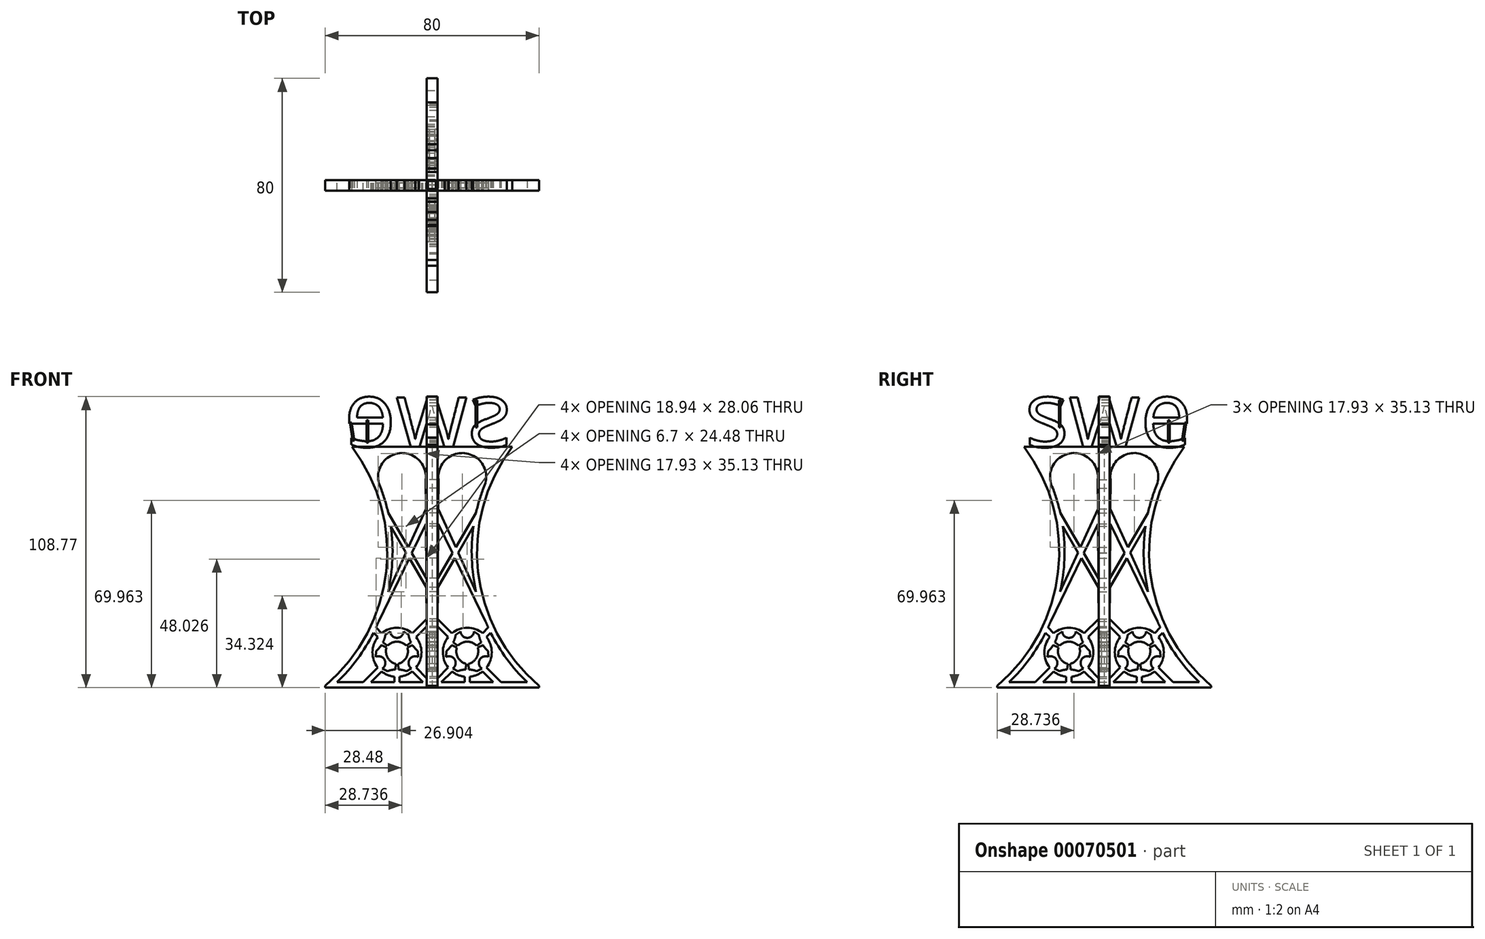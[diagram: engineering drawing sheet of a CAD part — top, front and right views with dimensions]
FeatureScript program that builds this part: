
annotation { "Feature Type Name" : "Feature", "Feature Type Description" : "" }
export const myFeature = defineFeature(function(context is Context, id is Id, definition is map)
    precondition{}
    {
        {
            var Q0;
            Q0=qCreatedBy(makeId("Right.planeOp"),FACE);
            var sketch = newSketch(context, id + "F0", { "sketchPlane" : qUnion([Q0])});
            skLineSegment(sketch, "E0", {"start": v(-30, 90) * mm, "end": v(0, 90) * mm});
            skLineSegment(sketch, "E1", {"start": v(0, 90) * mm, "end": v(0, 0) * mm});
            skLineSegment(sketch, "E2", {"start": v(0, 0) * mm, "end": v(-40, 0) * mm});
            skLineSegment(sketch, "E3", {"start": v(-40, 0) * mm, "end": v(-40, 0.68) * mm});
            skArc(sketch, "E4", {"start": v(-40, 0.68) * mm, "mid": v(-17.2, 43.35) * mm, "end": v(-30, 90) * mm});
            skArc(sketch, "E5", {"start": v(-6.02, 7.42) * mm, "mid": v(-4, 13.15) * mm, "end": v(-6.01, 18.88) * mm});
            skArc(sketch, "E6.0", {"start": v(-35.54, 2) * mm, "mid": v(-27.93, 10.66) * mm, "end": v(-21.9, 20.5) * mm});
            skLineSegment(sketch, "E6.1", {"start": v(-2, 2) * mm, "end": v(-12.16, 2) * mm});
            skLineSegment(sketch, "E7", {"start": v(-25.73, 2) * mm, "end": v(-20.3, 7.43) * mm});
            skLineSegment(sketch, "E8", {"start": v(-22.9, 2) * mm, "end": v(-18.89, 6.02) * mm});
            skLineSegment(sketch, "E9", {"start": v(-2, 3.4) * mm, "end": v(-6.02, 7.42) * mm});
            skLineSegment(sketch, "E10", {"start": v(-3.42, 2) * mm, "end": v(-7.43, 6.01) * mm});
            skLineSegment(sketch, "E11.trimOffspring", {"start": v(-7.42, 20.3) * mm, "end": v(-2.05, 25.66) * mm});
            skLineSegment(sketch, "E12.trimOffspring", {"start": v(-6.01, 18.88) * mm, "end": v(-2, 22.89) * mm});
            skLineSegment(sketch, "E13.trimOffspring", {"start": v(-18.88, 20.3) * mm, "end": v(-20.99, 22.4) * mm});
            skLineSegment(sketch, "E14.trimOffspring", {"start": v(-20.3, 18.89) * mm, "end": v(-21.9, 20.5) * mm});
            skArc(sketch, "E15.trimOffspring", {"start": v(-18.89, 6.02) * mm, "mid": v(-16.66, 4.7) * mm, "end": v(-14.16, 4.05) * mm});
            skArc(sketch, "E16.trimOffspring", {"start": v(-20.3, 18.89) * mm, "mid": v(-22.31, 13.16) * mm, "end": v(-20.3, 7.43) * mm});
            skArc(sketch, "E17.trimOffspring", {"start": v(-7.42, 20.3) * mm, "mid": v(-13.15, 22.31) * mm, "end": v(-18.88, 20.3) * mm});
            skLineSegment(sketch, "E18.trimOffspring", {"start": v(-2, 22.89) * mm, "end": v(-2, 2) * mm});
            skLineSegment(sketch, "E19", {"start": v(-14.16, 4.05) * mm, "end": v(-14.16, 2) * mm});
            skLineSegment(sketch, "E20", {"start": v(-12.16, 4.05) * mm, "end": v(-12.16, 2) * mm});
            skPoint(sketch, "E20.startSnap0", {"position": v(-14.16, 4.05) * mm});
            skArc(sketch, "E21.trimOffspring", {"start": v(-12.16, 4.05) * mm, "mid": v(-9.65, 4.7) * mm, "end": v(-7.43, 6.01) * mm});
            skLineSegment(sketch, "E22.trimOffspring", {"start": v(-14.16, 2) * mm, "end": v(-35.54, 2) * mm});
            skLineSegment(sketch, "E23", {"start": v(-25.35, 13.16) * mm, "end": v(3.04, 13.16) * mm, "construction": true});
            skLineSegment(sketch, "E24", {"start": v(-13.16, 13.16) * mm, "end": v(-0.47, 22.2) * mm, "construction": true});
            skLineSegment(sketch, "E25", {"start": v(-13.16, 13.16) * mm, "end": v(-2.45, 29.33) * mm, "construction": true});
            skLineSegment(sketch, "E26", {"start": v(-13.16, 13.16) * mm, "end": v(-8.24, 28.3) * mm, "construction": true});
            skLineSegment(sketch, "E27", {"start": v(-9.65, 15.66) * mm, "end": v(-7.9, 16.9) * mm});
            skLineSegment(sketch, "E28", {"start": v(-10.64, 20.91) * mm, "end": v(-8.82, 19.7) * mm});
            skArc(sketch, "E29", {"start": v(-8.82, 19.7) * mm, "mid": v(-8.49, 18.27) * mm, "end": v(-7.9, 16.9) * mm});
            skLineSegment(sketch, "E30", {"start": v(-13.16, 13.16) * mm, "end": v(-18.41, 16.9) * mm, "construction": true});
            skLineSegment(sketch, "E31", {"start": v(-13.16, 13.16) * mm, "end": v(-18.55, 21.3) * mm, "construction": true});
            skLineSegment(sketch, "E32", {"start": v(-13.16, 13.16) * mm, "end": v(-16.83, 24.47) * mm, "construction": true});
            skLineSegment(sketch, "E33", {"start": v(-16.66, 15.66) * mm, "end": v(-18.41, 16.9) * mm});
            skLineSegment(sketch, "E34", {"start": v(-15.68, 20.91) * mm, "end": v(-17.5, 19.7) * mm});
            skArc(sketch, "E35", {"start": v(-15.68, 20.91) * mm, "mid": v(-13.16, 18.56) * mm, "end": v(-10.64, 20.91) * mm});
            skArc(sketch, "E36", {"start": v(-18.41, 16.9) * mm, "mid": v(-17.83, 18.27) * mm, "end": v(-17.5, 19.7) * mm});
            skArc(sketch, "E37", {"start": v(-9.65, 15.66) * mm, "mid": v(-13.16, 17.16) * mm, "end": v(-16.66, 15.66) * mm});
            skLineSegment(sketch, "E38", {"start": v(-25.53, 20.8) * mm, "end": v(-2.82, 20.8) * mm, "construction": true});
            skLineSegment(sketch, "E39", {"start": v(-16.66, 15.66) * mm, "end": v(-2.86, 15.66) * mm, "construction": true});
            skArc(sketch, "E40.1.0", {"start": v(-18.61, 7.1) * mm, "mid": v(-17.84, 10.45) * mm, "end": v(-21.13, 11.46) * mm});
            skLineSegment(sketch, "E40.1.1", {"start": v(-18.61, 7.1) * mm, "end": v(-16.66, 6.12) * mm});
            skArc(sketch, "E40.1.2", {"start": v(-13.77, 6.72) * mm, "mid": v(-15.25, 6.56) * mm, "end": v(-16.66, 6.12) * mm});
            skLineSegment(sketch, "E40.1.3", {"start": v(-13.57, 8.86) * mm, "end": v(-13.77, 6.72) * mm});
            skArc(sketch, "E40.1.4", {"start": v(-17.08, 14.94) * mm, "mid": v(-16.62, 11.15) * mm, "end": v(-13.57, 8.86) * mm});
            skLineSegment(sketch, "E40.1.5", {"start": v(-17.08, 14.94) * mm, "end": v(-19.03, 15.83) * mm});
            skArc(sketch, "E40.1.6", {"start": v(-21, 13.64) * mm, "mid": v(-19.92, 14.64) * mm, "end": v(-19.03, 15.83) * mm});
            skLineSegment(sketch, "E40.1.7", {"start": v(-21.13, 11.46) * mm, "end": v(-21, 13.64) * mm});
            skArc(sketch, "E40.2.0", {"start": v(-5.18, 11.46) * mm, "mid": v(-8.47, 10.45) * mm, "end": v(-7.7, 7.1) * mm});
            skLineSegment(sketch, "E40.2.1", {"start": v(-5.18, 11.46) * mm, "end": v(-5.31, 13.64) * mm});
            skArc(sketch, "E40.2.2", {"start": v(-7.28, 15.83) * mm, "mid": v(-6.4, 14.64) * mm, "end": v(-5.31, 13.64) * mm});
            skLineSegment(sketch, "E40.2.3", {"start": v(-9.23, 14.94) * mm, "end": v(-7.28, 15.83) * mm});
            skArc(sketch, "E40.2.4", {"start": v(-12.74, 8.86) * mm, "mid": v(-9.7, 11.15) * mm, "end": v(-9.23, 14.94) * mm});
            skLineSegment(sketch, "E40.2.5", {"start": v(-12.74, 8.86) * mm, "end": v(-12.54, 6.72) * mm});
            skArc(sketch, "E40.2.6", {"start": v(-9.65, 6.12) * mm, "mid": v(-11.06, 6.56) * mm, "end": v(-12.54, 6.72) * mm});
            skLineSegment(sketch, "E40.2.7", {"start": v(-7.7, 7.1) * mm, "end": v(-9.65, 6.12) * mm});
            skLineSegment(sketch, "E41", {"start": v(-2.37, 77.68) * mm, "end": v(-2.14, 40.93) * mm});
            skArc(sketch, "E42.trimOffspring", {"start": v(-35.54, 2) * mm, "mid": v(-26.56, 12.58) * mm, "end": v(-19.95, 24.78) * mm});
            skArc(sketch, "E43", {"start": v(-2.37, 77.68) * mm, "mid": v(-12.93, 87.53) * mm, "end": v(-19.17, 74.5) * mm});
            skLineSegment(sketch, "E44", {"start": v(-16.45, 35.79) * mm, "end": v(-9.74, 50.45) * mm});
            skLineSegment(sketch, "E45", {"start": v(-2.27, 61.23) * mm, "end": v(-7.6, 50.24) * mm});
            skLineSegment(sketch, "E46", {"start": v(-16.42, 65.3) * mm, "end": v(-8.86, 52.4) * mm});
            skLineSegment(sketch, "E47", {"start": v(-2.12, 37.44) * mm, "end": v(-8.51, 48.35) * mm});
            skArc(sketch, "E48.trimOffspring", {"start": v(-16.42, 65.3) * mm, "mid": v(-17.63, 69.95) * mm, "end": v(-19.17, 74.5) * mm});
            skLineSegment(sketch, "E49.trimOffspring", {"start": v(-8.86, 52.4) * mm, "end": v(-2.3, 66.74) * mm});
            skLineSegment(sketch, "E50.trimOffspring", {"start": v(-9.74, 50.45) * mm, "end": v(-15.49, 60.26) * mm});
            skLineSegment(sketch, "E51.trimOffspring", {"start": v(-7.6, 50.24) * mm, "end": v(-2.14, 40.93) * mm});
            skLineSegment(sketch, "E52.trimOffspring", {"start": v(-2.12, 37.44) * mm, "end": v(-2.05, 25.66) * mm});
            skArc(sketch, "E53.trimOffspring", {"start": v(-16.45, 35.79) * mm, "mid": v(-14.85, 47.98) * mm, "end": v(-15.49, 60.26) * mm});
            skLineSegment(sketch, "E54.trimOffspring", {"start": v(-8.51, 48.35) * mm, "end": v(-19.95, 24.78) * mm});
            skSolve(sketch);
        }
        {
            var Q0;
            Q0=qSketchRegion(id+"F0",true);
            extrude(context, id + "F1", {"entities" : qUnion([Q0]), "depth" : 2 * mm, "hasSecondDirection" : true, "secondDirectionOppositeDirection" : true, "secondDirectionDepth" : 2 * mm});
        }
        {
            var Q0;
            Q0=qCreatedBy(makeId("Right.planeOp"),FACE);
            var sketch = newSketch(context, id + "F2", { "sketchPlane" : qUnion([Q0])});
            skLineSegment(sketch, "E55", {"start": v(0, 81) * mm, "end": v(0, -28.5) * mm, "construction": true});
            skSolve(sketch);
        }
        {
            var Q0;
            Q0=makeQuery(id+"F1.opExtrude","SWEPT_BODY",BODY,{"disambiguationData":[OSD([sQuery(id+"F0.wireOp",EDGE,"E0"),sQuery(id+"F0.wireOp",EDGE,"E1"),sQuery(id+"F0.wireOp",EDGE,"N8EfN9Iy-VFxy-i62X-S3Tn-et34u0hB6ofw"),sQuery(id+"F0.wireOp",EDGE,"ofOerVMI-8AtS-AqWo-Xm8z-ZVAlB3EUovam"),sQuery(id+"F0.wireOp",EDGE,"ba3e6201-bb00-4176-be12-0bcf97df4df2"),sQuery(id+"F0.wireOp",EDGE,"k6Ju8hmT-RXya-gFIe-6RDm-fDKX84Fwp2G4"),sQuery(id+"F0.wireOp",EDGE,"dTDJtstR-zKxY-rc8w-sIGn-4ASnDpw26A23"),sQuery(id+"F0.wireOp",EDGE,"Cvr0LfUC-tO0D-IxcI-B5Ti-WW2sAGeSHFF8"),sQuery(id+"F0.wireOp",EDGE,"DwRJblST-1CEV-pcTT-NFQT-YytcCcE5cTGx"),sQuery(id+"F0.wireOp",EDGE,"973229ff-babc-457a-ac66-6eeaf75bea45")])]});
            var Q1;
            Q1=sQuery(id+"F2.wireOp",EDGE,"E55");
            circularPattern(context, id + "F3", {"entities" : qUnion([Q0]), "axis" : qUnion([Q1]), "angle" : 90 * degree, "instanceCount" : round(4)});
        }
        {
            var Q0;
            Q0=qCreatedBy(makeId("Right.planeOp"),FACE);
            var sketch = newSketch(context, id + "F4", { "sketchPlane" : qUnion([Q0])});
            skText(sketch, "E56", { "text": "swe", "fontName": "OpenSans-Regular.ttf"});
            skLineSegment(sketch, "E57", {"start": v(-2.01, 88.78) * mm, "end": v(-2.01, 87.76) * mm, "construction": true});
            skLineSegment(sketch, "E58", {"start": v(2.01, 88.85) * mm, "end": v(2.01, 87.7) * mm, "construction": true});
            skLineSegment(sketch, "E59", {"start": v(-2.01, 88.27) * mm, "end": v(0, 88.27) * mm, "construction": true});
            skPoint(sketch, "E59.endSnap0", {"position": v(-2.01, 88.27) * mm});
            skLineSegment(sketch, "E60", {"start": v(0, 88.27) * mm, "end": v(2.01, 88.27) * mm, "construction": true});
            skLineSegment(sketch, "E61", {"start": v(0, 88.27) * mm, "end": v(0, 111.2) * mm, "construction": true});
            const initialGuessF4  = {"E56": [-0.0297, 0.09, 1, 0, 0.0248]};
            skSetInitialGuess(sketch, initialGuessF4);
            skSolve(sketch);
        }
        {
            var Q0;
            Q0=qSketchRegion(id+"F4",true);
            var Q1;
            Q1=makeQuery(id+"F1.opExtrude","CAP_FACE",FACE,{"disambiguationData":[OSD([sQuery(id+"F0.wireOp",EDGE,"E0"),sQuery(id+"F0.wireOp",EDGE,"E1"),sQuery(id+"F0.wireOp",EDGE,"E2"),sQuery(id+"F0.wireOp",EDGE,"E3"),sQuery(id+"F0.wireOp",EDGE,"E4"),sQuery(id+"F0.wireOp",EDGE,"E5"),sQuery(id+"F0.wireOp",EDGE,"E6.1"),sQuery(id+"F0.wireOp",EDGE,"E7"),sQuery(id+"F0.wireOp",EDGE,"E8"),sQuery(id+"F0.wireOp",EDGE,"E9"),sQuery(id+"F0.wireOp",EDGE,"E10"),sQuery(id+"F0.wireOp",EDGE,"E11.trimOffspring"),sQuery(id+"F0.wireOp",EDGE,"E12.trimOffspring"),sQuery(id+"F0.wireOp",EDGE,"E13.trimOffspring"),sQuery(id+"F0.wireOp",EDGE,"E14.trimOffspring"),sQuery(id+"F0.wireOp",EDGE,"E15.trimOffspring"),sQuery(id+"F0.wireOp",EDGE,"E16.trimOffspring"),sQuery(id+"F0.wireOp",EDGE,"E17.trimOffspring"),sQuery(id+"F0.wireOp",EDGE,"E18.trimOffspring"),sQuery(id+"F0.wireOp",EDGE,"E19"),sQuery(id+"F0.wireOp",EDGE,"E20"),sQuery(id+"F0.wireOp",EDGE,"E21.trimOffspring"),sQuery(id+"F0.wireOp",EDGE,"E22.trimOffspring"),sQuery(id+"F0.wireOp",EDGE,"E27"),sQuery(id+"F0.wireOp",EDGE,"E28"),sQuery(id+"F0.wireOp",EDGE,"E29"),sQuery(id+"F0.wireOp",EDGE,"E33"),sQuery(id+"F0.wireOp",EDGE,"E34"),sQuery(id+"F0.wireOp",EDGE,"E35"),sQuery(id+"F0.wireOp",EDGE,"E36"),sQuery(id+"F0.wireOp",EDGE,"E37"),sQuery(id+"F0.wireOp",EDGE,"E40.1.0"),sQuery(id+"F0.wireOp",EDGE,"E40.1.1"),sQuery(id+"F0.wireOp",EDGE,"E40.1.2"),sQuery(id+"F0.wireOp",EDGE,"E40.1.3"),sQuery(id+"F0.wireOp",EDGE,"E40.1.4"),sQuery(id+"F0.wireOp",EDGE,"E40.1.5"),sQuery(id+"F0.wireOp",EDGE,"E40.1.6"),sQuery(id+"F0.wireOp",EDGE,"E40.1.7"),sQuery(id+"F0.wireOp",EDGE,"E40.2.0"),sQuery(id+"F0.wireOp",EDGE,"E40.2.1"),sQuery(id+"F0.wireOp",EDGE,"E40.2.2"),sQuery(id+"F0.wireOp",EDGE,"E40.2.3"),sQuery(id+"F0.wireOp",EDGE,"E40.2.4"),sQuery(id+"F0.wireOp",EDGE,"E40.2.5"),sQuery(id+"F0.wireOp",EDGE,"E40.2.6"),sQuery(id+"F0.wireOp",EDGE,"E40.2.7"),sQuery(id+"F0.wireOp",EDGE,"E41"),sQuery(id+"F0.wireOp",EDGE,"E42.trimOffspring"),sQuery(id+"F0.wireOp",EDGE,"E43")])],"isStart":false});
            var Q2;
            Q2=makeQuery(id+"F1.opExtrude","CAP_FACE",FACE,{"disambiguationData":[OSD([sQuery(id+"F0.wireOp",EDGE,"E0"),sQuery(id+"F0.wireOp",EDGE,"E1"),sQuery(id+"F0.wireOp",EDGE,"E2"),sQuery(id+"F0.wireOp",EDGE,"E3"),sQuery(id+"F0.wireOp",EDGE,"E4"),sQuery(id+"F0.wireOp",EDGE,"E5"),sQuery(id+"F0.wireOp",EDGE,"E6.1"),sQuery(id+"F0.wireOp",EDGE,"E7"),sQuery(id+"F0.wireOp",EDGE,"E8"),sQuery(id+"F0.wireOp",EDGE,"E9"),sQuery(id+"F0.wireOp",EDGE,"E10"),sQuery(id+"F0.wireOp",EDGE,"E11.trimOffspring"),sQuery(id+"F0.wireOp",EDGE,"E12.trimOffspring"),sQuery(id+"F0.wireOp",EDGE,"E13.trimOffspring"),sQuery(id+"F0.wireOp",EDGE,"E14.trimOffspring"),sQuery(id+"F0.wireOp",EDGE,"E15.trimOffspring"),sQuery(id+"F0.wireOp",EDGE,"E16.trimOffspring"),sQuery(id+"F0.wireOp",EDGE,"E17.trimOffspring"),sQuery(id+"F0.wireOp",EDGE,"E18.trimOffspring"),sQuery(id+"F0.wireOp",EDGE,"E19"),sQuery(id+"F0.wireOp",EDGE,"E20"),sQuery(id+"F0.wireOp",EDGE,"E21.trimOffspring"),sQuery(id+"F0.wireOp",EDGE,"E22.trimOffspring"),sQuery(id+"F0.wireOp",EDGE,"E27"),sQuery(id+"F0.wireOp",EDGE,"E28"),sQuery(id+"F0.wireOp",EDGE,"E29"),sQuery(id+"F0.wireOp",EDGE,"E33"),sQuery(id+"F0.wireOp",EDGE,"E34"),sQuery(id+"F0.wireOp",EDGE,"E35"),sQuery(id+"F0.wireOp",EDGE,"E36"),sQuery(id+"F0.wireOp",EDGE,"E37"),sQuery(id+"F0.wireOp",EDGE,"E40.1.0"),sQuery(id+"F0.wireOp",EDGE,"E40.1.1"),sQuery(id+"F0.wireOp",EDGE,"E40.1.2"),sQuery(id+"F0.wireOp",EDGE,"E40.1.3"),sQuery(id+"F0.wireOp",EDGE,"E40.1.4"),sQuery(id+"F0.wireOp",EDGE,"E40.1.5"),sQuery(id+"F0.wireOp",EDGE,"E40.1.6"),sQuery(id+"F0.wireOp",EDGE,"E40.1.7"),sQuery(id+"F0.wireOp",EDGE,"E40.2.0"),sQuery(id+"F0.wireOp",EDGE,"E40.2.1"),sQuery(id+"F0.wireOp",EDGE,"E40.2.2"),sQuery(id+"F0.wireOp",EDGE,"E40.2.3"),sQuery(id+"F0.wireOp",EDGE,"E40.2.4"),sQuery(id+"F0.wireOp",EDGE,"E40.2.5"),sQuery(id+"F0.wireOp",EDGE,"E40.2.6"),sQuery(id+"F0.wireOp",EDGE,"E40.2.7"),sQuery(id+"F0.wireOp",EDGE,"E41"),sQuery(id+"F0.wireOp",EDGE,"E42.trimOffspring"),sQuery(id+"F0.wireOp",EDGE,"E43")])],"isStart":true});
            extrude(context, id + "F5", {"entities" : qUnion([Q0]), "endBound" : BoundingType.UP_TO_SURFACE, "endBoundEntityFace" : qUnion([Q1]), "depth" : .5 * mm, "hasSecondDirection" : true, "secondDirectionBound" : SecondDirectionBoundingType.UP_TO_SURFACE, "secondDirectionOppositeDirection" : true, "secondDirectionBoundEntityFace" : qUnion([Q2]), "secondDirectionDepth" : .5 * mm});
        }
        {
            var Q0;
            Q0=qCreatedBy(makeId("Right.planeOp"),FACE);
            var sketch = newSketch(context, id + "F6", { "sketchPlane" : qUnion([Q0])});
            skLineSegment(sketch, "E62", {"start": v(0, 67.06) * mm, "end": v(0, 97.37) * mm, "construction": true});
            skSolve(sketch);
        }
        {
            var Q0;
            Q0=qCreatedBy(makeId("Right.planeOp"),FACE);
            var sketch = newSketch(context, id + "F7", { "sketchPlane" : qUnion([Q0])});
            skLineSegment(sketch, "E63.bottom", {"start": v(-16.91, 107.4) * mm, "end": v(-16.31, 107.4) * mm});
            skLineSegment(sketch, "E63.top", {"start": v(-16.91, 97.32) * mm, "end": v(-16.31, 97.32) * mm});
            skLineSegment(sketch, "E63.left", {"start": v(-16.91, 107.4) * mm, "end": v(-16.91, 97.32) * mm});
            skLineSegment(sketch, "E63.right", {"start": v(-16.31, 107.4) * mm, "end": v(-16.31, 97.32) * mm});
            skLineSegment(sketch, "E64.bottom", {"start": v(30.15, 99.1) * mm, "end": v(30.75, 99.1) * mm});
            skLineSegment(sketch, "E64.top", {"start": v(29.11, 92.28) * mm, "end": v(29.71, 92.28) * mm});
            skLineSegment(sketch, "E64.left", {"start": v(30.15, 99.1) * mm, "end": v(29.11, 92.28) * mm});
            skLineSegment(sketch, "E64.right", {"start": v(30.75, 99.1) * mm, "end": v(29.71, 92.28) * mm});
            skLineSegment(sketch, "E65.bottom", {"start": v(23.9, 99.96) * mm, "end": v(24.5, 99.96) * mm});
            skLineSegment(sketch, "E65.top", {"start": v(23.9, 91.55) * mm, "end": v(24.5, 91.55) * mm});
            skLineSegment(sketch, "E65.left", {"start": v(23.9, 99.96) * mm, "end": v(23.9, 91.55) * mm});
            skLineSegment(sketch, "E65.right", {"start": v(24.5, 99.96) * mm, "end": v(24.5, 91.55) * mm});
            skSolve(sketch);
        }
        {
            var Q0;
            Q0 = qSketchRegion(id + "F7", true);
            var Q1;
            Q1=makeQuery(id+"F1.opExtrude","CAP_FACE",FACE,{"disambiguationData":[OSD([sQuery(id+"F0.wireOp",EDGE,"E0"),sQuery(id+"F0.wireOp",EDGE,"E1"),sQuery(id+"F0.wireOp",EDGE,"E2"),sQuery(id+"F0.wireOp",EDGE,"E3"),sQuery(id+"F0.wireOp",EDGE,"E4"),sQuery(id+"F0.wireOp",EDGE,"E5"),sQuery(id+"F0.wireOp",EDGE,"E6.1"),sQuery(id+"F0.wireOp",EDGE,"E7"),sQuery(id+"F0.wireOp",EDGE,"E8"),sQuery(id+"F0.wireOp",EDGE,"E9"),sQuery(id+"F0.wireOp",EDGE,"E10"),sQuery(id+"F0.wireOp",EDGE,"E11.trimOffspring"),sQuery(id+"F0.wireOp",EDGE,"E12.trimOffspring"),sQuery(id+"F0.wireOp",EDGE,"E13.trimOffspring"),sQuery(id+"F0.wireOp",EDGE,"E14.trimOffspring"),sQuery(id+"F0.wireOp",EDGE,"E15.trimOffspring"),sQuery(id+"F0.wireOp",EDGE,"E16.trimOffspring"),sQuery(id+"F0.wireOp",EDGE,"E17.trimOffspring"),sQuery(id+"F0.wireOp",EDGE,"E18.trimOffspring"),sQuery(id+"F0.wireOp",EDGE,"E19"),sQuery(id+"F0.wireOp",EDGE,"E20"),sQuery(id+"F0.wireOp",EDGE,"E21.trimOffspring"),sQuery(id+"F0.wireOp",EDGE,"E22.trimOffspring"),sQuery(id+"F0.wireOp",EDGE,"E27"),sQuery(id+"F0.wireOp",EDGE,"E28"),sQuery(id+"F0.wireOp",EDGE,"E29"),sQuery(id+"F0.wireOp",EDGE,"E33"),sQuery(id+"F0.wireOp",EDGE,"E34"),sQuery(id+"F0.wireOp",EDGE,"E35"),sQuery(id+"F0.wireOp",EDGE,"E36"),sQuery(id+"F0.wireOp",EDGE,"E37"),sQuery(id+"F0.wireOp",EDGE,"E40.1.0"),sQuery(id+"F0.wireOp",EDGE,"E40.1.1"),sQuery(id+"F0.wireOp",EDGE,"E40.1.2"),sQuery(id+"F0.wireOp",EDGE,"E40.1.3"),sQuery(id+"F0.wireOp",EDGE,"E40.1.4"),sQuery(id+"F0.wireOp",EDGE,"E40.1.5"),sQuery(id+"F0.wireOp",EDGE,"E40.1.6"),sQuery(id+"F0.wireOp",EDGE,"E40.1.7"),sQuery(id+"F0.wireOp",EDGE,"E40.2.0"),sQuery(id+"F0.wireOp",EDGE,"E40.2.1"),sQuery(id+"F0.wireOp",EDGE,"E40.2.2"),sQuery(id+"F0.wireOp",EDGE,"E40.2.3"),sQuery(id+"F0.wireOp",EDGE,"E40.2.4"),sQuery(id+"F0.wireOp",EDGE,"E40.2.5"),sQuery(id+"F0.wireOp",EDGE,"E40.2.6"),sQuery(id+"F0.wireOp",EDGE,"E40.2.7"),sQuery(id+"F0.wireOp",EDGE,"E41"),sQuery(id+"F0.wireOp",EDGE,"E42.trimOffspring"),sQuery(id+"F0.wireOp",EDGE,"E43")])],"isStart":false});
            var Q2;
            Q2=makeQuery(id+"F1.opExtrude","CAP_FACE",FACE,{"disambiguationData":[OSD([sQuery(id+"F0.wireOp",EDGE,"E0"),sQuery(id+"F0.wireOp",EDGE,"E1"),sQuery(id+"F0.wireOp",EDGE,"E2"),sQuery(id+"F0.wireOp",EDGE,"E3"),sQuery(id+"F0.wireOp",EDGE,"E4"),sQuery(id+"F0.wireOp",EDGE,"E5"),sQuery(id+"F0.wireOp",EDGE,"E6.1"),sQuery(id+"F0.wireOp",EDGE,"E7"),sQuery(id+"F0.wireOp",EDGE,"E8"),sQuery(id+"F0.wireOp",EDGE,"E9"),sQuery(id+"F0.wireOp",EDGE,"E10"),sQuery(id+"F0.wireOp",EDGE,"E11.trimOffspring"),sQuery(id+"F0.wireOp",EDGE,"E12.trimOffspring"),sQuery(id+"F0.wireOp",EDGE,"E13.trimOffspring"),sQuery(id+"F0.wireOp",EDGE,"E14.trimOffspring"),sQuery(id+"F0.wireOp",EDGE,"E15.trimOffspring"),sQuery(id+"F0.wireOp",EDGE,"E16.trimOffspring"),sQuery(id+"F0.wireOp",EDGE,"E17.trimOffspring"),sQuery(id+"F0.wireOp",EDGE,"E18.trimOffspring"),sQuery(id+"F0.wireOp",EDGE,"E19"),sQuery(id+"F0.wireOp",EDGE,"E20"),sQuery(id+"F0.wireOp",EDGE,"E21.trimOffspring"),sQuery(id+"F0.wireOp",EDGE,"E22.trimOffspring"),sQuery(id+"F0.wireOp",EDGE,"E27"),sQuery(id+"F0.wireOp",EDGE,"E28"),sQuery(id+"F0.wireOp",EDGE,"E29"),sQuery(id+"F0.wireOp",EDGE,"E33"),sQuery(id+"F0.wireOp",EDGE,"E34"),sQuery(id+"F0.wireOp",EDGE,"E35"),sQuery(id+"F0.wireOp",EDGE,"E36"),sQuery(id+"F0.wireOp",EDGE,"E37"),sQuery(id+"F0.wireOp",EDGE,"E40.1.0"),sQuery(id+"F0.wireOp",EDGE,"E40.1.1"),sQuery(id+"F0.wireOp",EDGE,"E40.1.2"),sQuery(id+"F0.wireOp",EDGE,"E40.1.3"),sQuery(id+"F0.wireOp",EDGE,"E40.1.4"),sQuery(id+"F0.wireOp",EDGE,"E40.1.5"),sQuery(id+"F0.wireOp",EDGE,"E40.1.6"),sQuery(id+"F0.wireOp",EDGE,"E40.1.7"),sQuery(id+"F0.wireOp",EDGE,"E40.2.0"),sQuery(id+"F0.wireOp",EDGE,"E40.2.1"),sQuery(id+"F0.wireOp",EDGE,"E40.2.2"),sQuery(id+"F0.wireOp",EDGE,"E40.2.3"),sQuery(id+"F0.wireOp",EDGE,"E40.2.4"),sQuery(id+"F0.wireOp",EDGE,"E40.2.5"),sQuery(id+"F0.wireOp",EDGE,"E40.2.6"),sQuery(id+"F0.wireOp",EDGE,"E40.2.7"),sQuery(id+"F0.wireOp",EDGE,"E41"),sQuery(id+"F0.wireOp",EDGE,"E42.trimOffspring"),sQuery(id+"F0.wireOp",EDGE,"E43")])],"isStart":true});
            extrude(context, id + "F8", {"entities" : qUnion([Q0]), "endBound" : BoundingType.UP_TO_SURFACE, "endBoundEntityFace" : qUnion([Q1]), "depth" : .25 * mm, "hasSecondDirection" : true, "secondDirectionBound" : SecondDirectionBoundingType.UP_TO_SURFACE, "secondDirectionOppositeDirection" : true, "secondDirectionBoundEntityFace" : qUnion([Q2]), "secondDirectionDepth" : .25 * mm});
        }
        {
            var Q0;
            Q0=makeQuery(id+"F5.opExtrude","SWEPT_BODY",BODY,{"disambiguationData":[OSD([sQuery(id+"F4.wireOp",EDGE,"E56.sketch_text.stroke-48"),sQuery(id+"F4.wireOp",EDGE,"E56.sketch_text.stroke-49"),sQuery(id+"F4.wireOp",EDGE,"E56.sketch_text.stroke-50"),sQuery(id+"F4.wireOp",EDGE,"E56.sketch_text.stroke-51"),sQuery(id+"F4.wireOp",EDGE,"E56.sketch_text.stroke-52"),sQuery(id+"F4.wireOp",EDGE,"E56.sketch_text.stroke-53"),sQuery(id+"F4.wireOp",EDGE,"E56.sketch_text.stroke-54"),sQuery(id+"F4.wireOp",EDGE,"E56.sketch_text.stroke-55"),sQuery(id+"F4.wireOp",EDGE,"E56.sketch_text.stroke-56"),sQuery(id+"F4.wireOp",EDGE,"E56.sketch_text.stroke-57"),sQuery(id+"F4.wireOp",EDGE,"E56.sketch_text.stroke-58"),sQuery(id+"F4.wireOp",EDGE,"E56.sketch_text.stroke-59"),sQuery(id+"F4.wireOp",EDGE,"E56.sketch_text.stroke-60"),sQuery(id+"F4.wireOp",EDGE,"E56.sketch_text.stroke-61"),sQuery(id+"F4.wireOp",EDGE,"E56.sketch_text.stroke-62"),sQuery(id+"F4.wireOp",EDGE,"E56.sketch_text.stroke-63"),sQuery(id+"F4.wireOp",EDGE,"E56.sketch_text.stroke-64"),sQuery(id+"F4.wireOp",EDGE,"E56.sketch_text.stroke-65"),sQuery(id+"F4.wireOp",EDGE,"E56.sketch_text.stroke-66")])]});
            var Q1;
            Q1=makeQuery(id+"F5.opExtrude","SWEPT_BODY",BODY,{"disambiguationData":[OSD([sQuery(id+"F4.wireOp",EDGE,"E56.sketch_text.stroke-25"),sQuery(id+"F4.wireOp",EDGE,"E56.sketch_text.stroke-26"),sQuery(id+"F4.wireOp",EDGE,"E56.sketch_text.stroke-27"),sQuery(id+"F4.wireOp",EDGE,"E56.sketch_text.stroke-28"),sQuery(id+"F4.wireOp",EDGE,"E56.sketch_text.stroke-29"),sQuery(id+"F4.wireOp",EDGE,"E56.sketch_text.stroke-30"),sQuery(id+"F4.wireOp",EDGE,"E56.sketch_text.stroke-31"),sQuery(id+"F4.wireOp",EDGE,"E56.sketch_text.stroke-32"),sQuery(id+"F4.wireOp",EDGE,"E56.sketch_text.stroke-33"),sQuery(id+"F4.wireOp",EDGE,"E56.sketch_text.stroke-34"),sQuery(id+"F4.wireOp",EDGE,"E56.sketch_text.stroke-35"),sQuery(id+"F4.wireOp",EDGE,"E56.sketch_text.stroke-36"),sQuery(id+"F4.wireOp",EDGE,"E56.sketch_text.stroke-37"),sQuery(id+"F4.wireOp",EDGE,"E56.sketch_text.stroke-38"),sQuery(id+"F4.wireOp",EDGE,"E56.sketch_text.stroke-39"),sQuery(id+"F4.wireOp",EDGE,"E56.sketch_text.stroke-40"),sQuery(id+"F4.wireOp",EDGE,"E56.sketch_text.stroke-41"),sQuery(id+"F4.wireOp",EDGE,"E56.sketch_text.stroke-42"),sQuery(id+"F4.wireOp",EDGE,"E56.sketch_text.stroke-43"),sQuery(id+"F4.wireOp",EDGE,"E56.sketch_text.stroke-44"),sQuery(id+"F4.wireOp",EDGE,"E56.sketch_text.stroke-45"),sQuery(id+"F4.wireOp",EDGE,"E56.sketch_text.stroke-46"),sQuery(id+"F4.wireOp",EDGE,"E56.sketch_text.stroke-47")])]});
            var Q2;
            Q2=makeQuery(id+"F5.opExtrude","SWEPT_BODY",BODY,{"disambiguationData":[OSD([sQuery(id+"F4.wireOp",EDGE,"E56.sketch_text.stroke-0"),sQuery(id+"F4.wireOp",EDGE,"E56.sketch_text.stroke-1"),sQuery(id+"F4.wireOp",EDGE,"E56.sketch_text.stroke-2"),sQuery(id+"F4.wireOp",EDGE,"E56.sketch_text.stroke-3"),sQuery(id+"F4.wireOp",EDGE,"E56.sketch_text.stroke-4"),sQuery(id+"F4.wireOp",EDGE,"E56.sketch_text.stroke-5"),sQuery(id+"F4.wireOp",EDGE,"E56.sketch_text.stroke-6"),sQuery(id+"F4.wireOp",EDGE,"E56.sketch_text.stroke-7"),sQuery(id+"F4.wireOp",EDGE,"E56.sketch_text.stroke-8"),sQuery(id+"F4.wireOp",EDGE,"E56.sketch_text.stroke-9"),sQuery(id+"F4.wireOp",EDGE,"E56.sketch_text.stroke-10"),sQuery(id+"F4.wireOp",EDGE,"E56.sketch_text.stroke-11"),sQuery(id+"F4.wireOp",EDGE,"E56.sketch_text.stroke-12"),sQuery(id+"F4.wireOp",EDGE,"E56.sketch_text.stroke-13"),sQuery(id+"F4.wireOp",EDGE,"E56.sketch_text.stroke-14"),sQuery(id+"F4.wireOp",EDGE,"E56.sketch_text.stroke-15"),sQuery(id+"F4.wireOp",EDGE,"E56.sketch_text.stroke-16"),sQuery(id+"F4.wireOp",EDGE,"E56.sketch_text.stroke-17"),sQuery(id+"F4.wireOp",EDGE,"E56.sketch_text.stroke-18"),sQuery(id+"F4.wireOp",EDGE,"E56.sketch_text.stroke-19"),sQuery(id+"F4.wireOp",EDGE,"E56.sketch_text.stroke-20"),sQuery(id+"F4.wireOp",EDGE,"E56.sketch_text.stroke-21"),sQuery(id+"F4.wireOp",EDGE,"E56.sketch_text.stroke-22"),sQuery(id+"F4.wireOp",EDGE,"E56.sketch_text.stroke-23"),sQuery(id+"F4.wireOp",EDGE,"E56.sketch_text.stroke-24")])]});
            var Q3;
            Q3=makeQuery(id+"F8.opExtrude","SWEPT_BODY",BODY,{"disambiguationData":[OSD([sQuery(id+"F7.wireOp",EDGE,"E63.bottom"),sQuery(id+"F7.wireOp",EDGE,"E63.top"),sQuery(id+"F7.wireOp",EDGE,"E63.left"),sQuery(id+"F7.wireOp",EDGE,"E63.right")])]});
            var Q4;
            Q4=makeQuery(id+"F8.opExtrude","SWEPT_BODY",BODY,{"disambiguationData":[OSD([sQuery(id+"F7.wireOp",EDGE,"5dc68fb5-edd3-4b79-a733-3356c3f042f6.bottom"),sQuery(id+"F7.wireOp",EDGE,"5dc68fb5-edd3-4b79-a733-3356c3f042f6.top"),sQuery(id+"F7.wireOp",EDGE,"5dc68fb5-edd3-4b79-a733-3356c3f042f6.left"),sQuery(id+"F7.wireOp",EDGE,"5dc68fb5-edd3-4b79-a733-3356c3f042f6.right")])]});
            var Q5;
            Q5=makeQuery(id+"F8.opExtrude","SWEPT_BODY",BODY,{"disambiguationData":[OSD([sQuery(id+"F7.wireOp",EDGE,"E64.bottom"),sQuery(id+"F7.wireOp",EDGE,"E64.top"),sQuery(id+"F7.wireOp",EDGE,"E64.left"),sQuery(id+"F7.wireOp",EDGE,"E64.right")])]});
            var Q6;
            Q6=makeQuery(id+"F8.opExtrude","SWEPT_BODY",BODY,{"disambiguationData":[OSD([sQuery(id+"F7.wireOp",EDGE,"E65.bottom"),sQuery(id+"F7.wireOp",EDGE,"E65.top"),sQuery(id+"F7.wireOp",EDGE,"E65.left"),sQuery(id+"F7.wireOp",EDGE,"E65.right")])]});
            var Q7;
            Q7=sQuery(id+"F6.wireOp",EDGE,"E62");
            circularPattern(context, id + "F9", {"entities" : qUnion([Q0, Q1, Q2, Q3, Q4, Q5, Q6]), "axis" : qUnion([Q7]), "angle" : 90 * degree, "instanceCount" : 2});
        }
        {
            var Q0;
            Q0=qCreatedBy(makeId("Right.planeOp"),FACE);
            var sketch = newSketch(context, id + "F10", { "sketchPlane" : qUnion([Q0])});
            skCircle(sketch, "E66", {"center": v(13.16, 13.16) * mm, "radius": 8.72 * mm});
            skLineSegment(sketch, "E67", {"start": v(0, -9.43) * mm, "end": v(0, 24.64) * mm, "construction": true});
            skSolve(sketch);
        }
        {
            var Q0;
            Q0=qCreatedBy(makeId("Right.planeOp"),FACE);
            var sketch = newSketch(context, id + "F11", { "sketchPlane" : qUnion([Q0])});
            skLineSegment(sketch, "E68", {"start": v(0, 7.6) * mm, "end": v(0, -25.74) * mm, "construction": true});
            skSolve(sketch);
        }
        {
            var Q0;
            Q0 = qSketchRegion(id + "F10", true);
            extrude(context, id + "F12", {"entities" : qUnion([Q0]), "operationType" : NewBodyOperationType.ADD, "depth" : 1 * mm, "hasSecondDirection" : true, "secondDirectionOppositeDirection" : true, "secondDirectionDepth" : 1 * mm});
        }
        {
            var Q0;
            Q0=makeQuery(id+"F3.opPattern","COPY",BODY,{"derivedFrom":makeQuery(id+"F1.opExtrude","SWEPT_BODY",BODY,{"disambiguationData":[OSD([sQuery(id+"F0.wireOp",EDGE,"E0"),sQuery(id+"F0.wireOp",EDGE,"E1"),sQuery(id+"F0.wireOp",EDGE,"E2"),sQuery(id+"F0.wireOp",EDGE,"E3"),sQuery(id+"F0.wireOp",EDGE,"E4"),sQuery(id+"F0.wireOp",EDGE,"E5"),sQuery(id+"F0.wireOp",EDGE,"E6.0"),sQuery(id+"F0.wireOp",EDGE,"E6.1"),sQuery(id+"F0.wireOp",EDGE,"E6.2"),sQuery(id+"F0.wireOp",EDGE,"E6.3"),sQuery(id+"F0.wireOp",EDGE,"E7"),sQuery(id+"F0.wireOp",EDGE,"E8"),sQuery(id+"F0.wireOp",EDGE,"E9"),sQuery(id+"F0.wireOp",EDGE,"E10"),sQuery(id+"F0.wireOp",EDGE,"E11.trimOffspring"),sQuery(id+"F0.wireOp",EDGE,"E12.trimOffspring"),sQuery(id+"F0.wireOp",EDGE,"E13.trimOffspring"),sQuery(id+"F0.wireOp",EDGE,"E14.trimOffspring"),sQuery(id+"F0.wireOp",EDGE,"E15.trimOffspring"),sQuery(id+"F0.wireOp",EDGE,"E16.trimOffspring"),sQuery(id+"F0.wireOp",EDGE,"f6aabd91-0355-4ce8-b6d2-6d85713953a7.trimOffspring"),sQuery(id+"F0.wireOp",EDGE,"E17.trimOffspring"),sQuery(id+"F0.wireOp",EDGE,"E18.trimOffspring"),sQuery(id+"F0.wireOp",EDGE,"E19"),sQuery(id+"F0.wireOp",EDGE,"E20"),sQuery(id+"F0.wireOp",EDGE,"E21.trimOffspring"),sQuery(id+"F0.wireOp",EDGE,"E22.trimOffspring"),sQuery(id+"F0.wireOp",EDGE,"E27"),sQuery(id+"F0.wireOp",EDGE,"E28"),sQuery(id+"F0.wireOp",EDGE,"E29"),sQuery(id+"F0.wireOp",EDGE,"E33"),sQuery(id+"F0.wireOp",EDGE,"E34"),sQuery(id+"F0.wireOp",EDGE,"E35"),sQuery(id+"F0.wireOp",EDGE,"E36"),sQuery(id+"F0.wireOp",EDGE,"E37"),sQuery(id+"F0.wireOp",EDGE,"E40.1.0"),sQuery(id+"F0.wireOp",EDGE,"E40.1.1"),sQuery(id+"F0.wireOp",EDGE,"E40.1.2"),sQuery(id+"F0.wireOp",EDGE,"E40.1.3"),sQuery(id+"F0.wireOp",EDGE,"E40.1.4"),sQuery(id+"F0.wireOp",EDGE,"E40.1.5"),sQuery(id+"F0.wireOp",EDGE,"E40.1.6"),sQuery(id+"F0.wireOp",EDGE,"E40.1.7"),sQuery(id+"F0.wireOp",EDGE,"E40.2.0"),sQuery(id+"F0.wireOp",EDGE,"E40.2.1"),sQuery(id+"F0.wireOp",EDGE,"E40.2.2"),sQuery(id+"F0.wireOp",EDGE,"E40.2.3"),sQuery(id+"F0.wireOp",EDGE,"E40.2.4"),sQuery(id+"F0.wireOp",EDGE,"E40.2.5"),sQuery(id+"F0.wireOp",EDGE,"E40.2.6"),sQuery(id+"F0.wireOp",EDGE,"E40.2.7")])]}),"instanceName":"2"});
            var Q1;
            Q1=sQuery(id+"F11.wireOp",EDGE,"E68");
            circularPattern(context, id + "F13", {"entities" : qUnion([Q0]), "axis" : qUnion([Q1]), "angle" : 90 * degree, "instanceCount" : 4});
        }
    });
